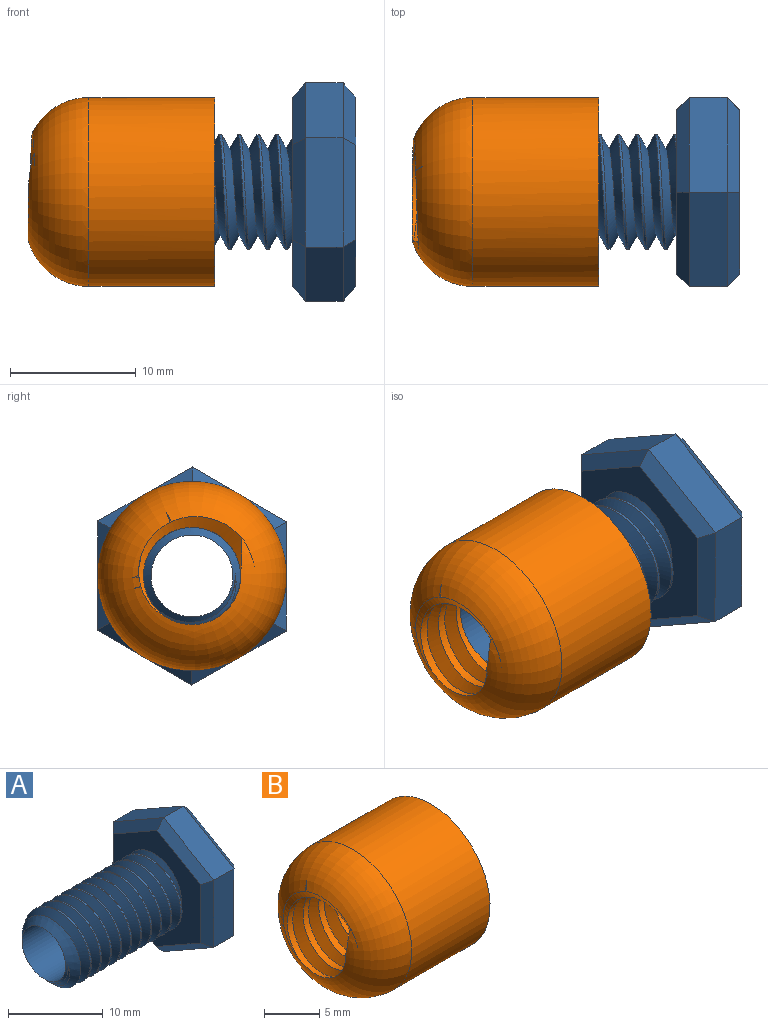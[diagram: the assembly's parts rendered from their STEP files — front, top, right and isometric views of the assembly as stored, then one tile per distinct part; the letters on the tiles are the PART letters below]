
ASSEMBLY  parts=2 mates=1
PART A: 26 faces, bbox 23.2x15.9x18.1 mm
  f0: cylinder r=4.56mm len=15.5mm, axis (1,0,0), area 47.8mm2, adj f1,f2,f3,f4,f12
  f1: bspline ~17.66x10.53mm, area 351.9mm2, adj f0,f2,f3,f4,f12
  f2: bspline ~18.16x10.53mm, area 351.7mm2, adj f0,f1,f3,f12
  f3: cone r=4.56mm half-angle=45deg, axis (1,0,0), area 26.7mm2, adj f0,f1,f2,f4,f25
  f4: cone r=4.56mm half-angle=45deg, axis (1,0,0), area 0.3mm2, adj f0,f1,f3
  f5: plane 7.48x4.37mm, normal (0,-0.5,0.86), area 26mm2, adj f6,f10,f18,f22
  f6: plane 8.66x3mm, normal (0,-1,0), area 26mm2, adj f5,f7,f16,f20
  f7: plane 7.52x4.29mm, normal (0,-0.5,-0.87), area 26mm2, adj f6,f8,f14,f19
  f8: plane 7.48x4.37mm, normal (0,0.5,-0.86), area 26mm2, adj f7,f9,f13,f21
  f9: plane 8.66x3mm, normal (0,1,0), area 26mm2, adj f8,f10,f15,f23
  f10: plane 7.52x4.29mm, normal (0,0.5,0.87), area 26mm2, adj f5,f9,f17,f24
  f11: plane 15.01x13.04mm, normal (1,0,0), area 113.2mm2, adj f13,f14,f15,f16,f17,f18,f25
  f12: plane 15.83x13.86mm, normal (-1,0,0), area 94.1mm2, adj f0,f1,f2,f19,f20,f21,f22,f23
  f13: plane 7.48x4.94mm, normal (0.71,0.36,-0.61), area 11.4mm2, adj f8,f11,f14,f15
  f14: plane 7.52x4.88mm, normal (0.71,-0.35,-0.61), area 11.4mm2, adj f7,f11,f13,f16
  f15: plane 8.66x1.04mm, normal (0.71,0.71,0), area 11.4mm2, adj f9,f11,f13,f17
  f16: plane 8.66x1.04mm, normal (0.71,-0.71,0), area 11.4mm2, adj f6,f11,f14,f18
  f17: plane 7.52x4.88mm, normal (0.71,0.35,0.61), area 11.4mm2, adj f10,f11,f15,f18
  f18: plane 7.48x4.94mm, normal (0.71,-0.36,0.61), area 11.4mm2, adj f5,f11,f16,f17
  f19: plane 7.52x4.88mm, normal (-0.71,-0.35,-0.61), area 11.4mm2, adj f7,f12,f20,f21
  f20: plane 8.66x1.04mm, normal (-0.71,-0.71,0), area 11.4mm2, adj f6,f12,f19,f22
  f21: plane 7.48x4.94mm, normal (-0.71,0.36,-0.61), area 11.4mm2, adj f8,f12,f19,f23
  f22: plane 7.48x4.94mm, normal (-0.71,-0.36,0.61), area 11.4mm2, adj f5,f12,f20,f24
  f23: plane 8.66x1.04mm, normal (-0.71,0.71,0), area 11.4mm2, adj f9,f12,f21,f24
  f24: plane 7.52x4.88mm, normal (-0.71,0.35,0.61), area 11.4mm2, adj f10,f12,f22,f23
  f25: cylinder r=3.25mm len=21.81mm, axis (1,0,0), area 445.4mm2, adj f3,f11
PART B: 6 faces, bbox 16.9x15.6x15.6 mm
  f0: cylinder r=3.86mm len=14.81mm, axis (1,0,0), area 130.6mm2, adj f2,f3,f4,f5
  f1: cylinder r=7.5mm len=15mm, axis (1,0,0), area 471.2mm2, adj f2,f5
  f2: plane 15.6x15.6mm, normal (1,0,0), area 120.2mm2, adj f0,f1,f3,f4
  f3: bspline ~15.98x11.51mm, area 261.2mm2, adj f0,f2,f4,f5
  f4: bspline ~16.32x11.51mm, area 263.1mm2, adj f0,f2,f3,f5
  f5: torus R=2.5mm, axis (1,0,0), area 242.4mm2, adj f0,f1,f3,f4
PLACE A t=(0,6.45,-1)mm fixed
PLACE B rot(axis=(-1,0,0),1.9deg) t=(-8.68,6.45,-1)mm
MATE cylindrical B.f0 <-> A.f25  axis (1,0,0) through (-13.68,6.45,-1)mm
